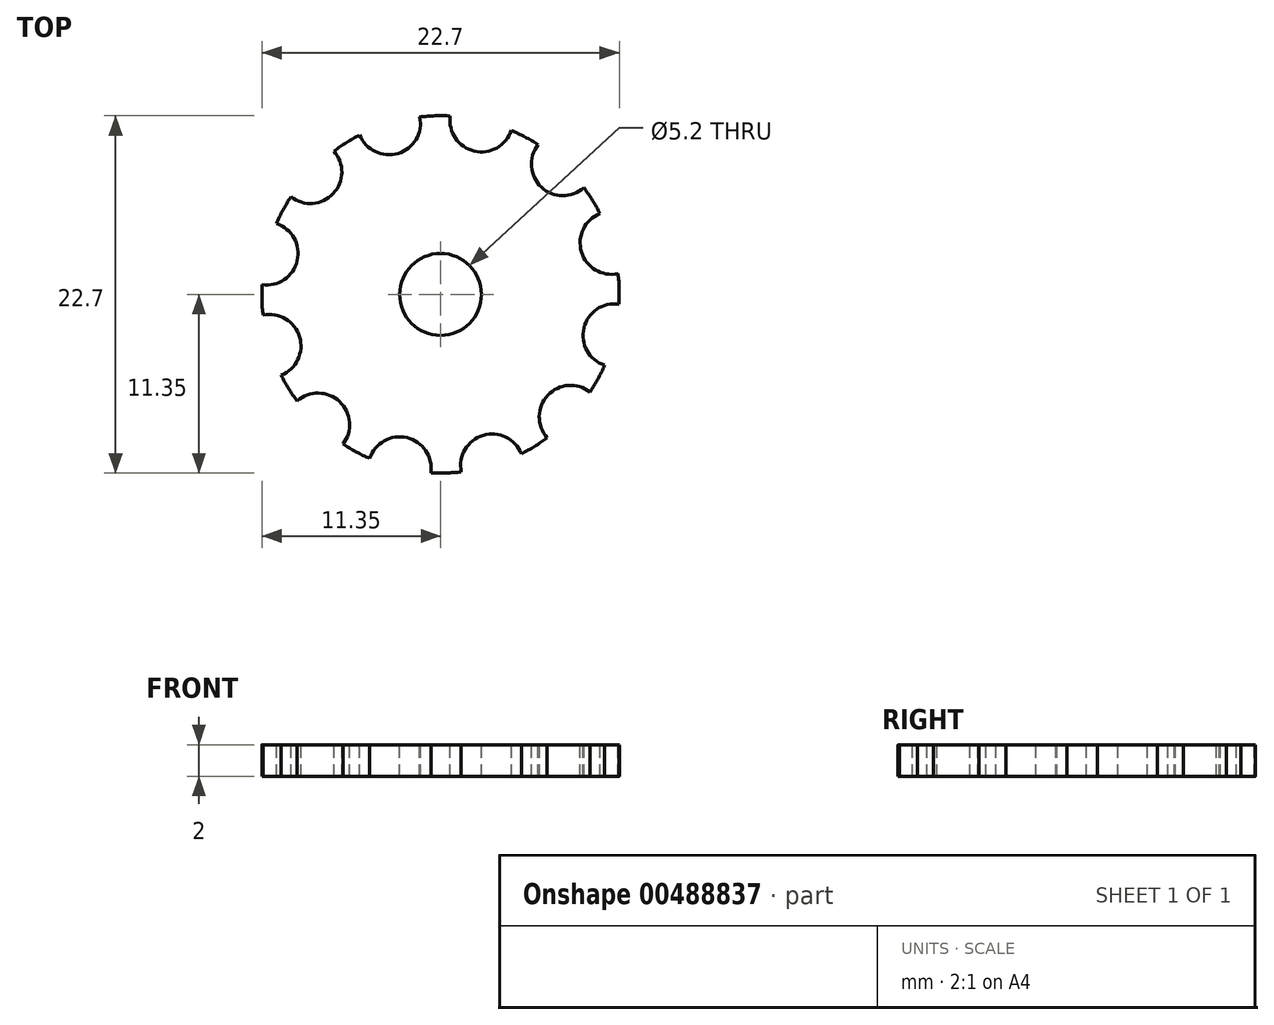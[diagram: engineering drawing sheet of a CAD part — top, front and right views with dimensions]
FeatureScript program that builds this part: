
annotation { "Feature Type Name" : "Feature", "Feature Type Description" : "" }
export const myFeature = defineFeature(function(context is Context, id is Id, definition is map)
    precondition{}
    {
        {
            var Q0;
            Q0=qCreatedBy(makeId("Top.planeOp"),FACE);
            var sketch = newSketch(context, id + "F0", { "sketchPlane" : qUnion([Q0])});
            skCircle(sketch, "E0", {"center": v(0, 0) * mm, "radius": 11.35 * mm});
            skSolve(sketch);
        }
        {
            var Q0;
            Q0=makeQuery(id+"F0.imprint","IMPRINT",FACE,{"disambiguationData":[TD([[makeQuery(id+"F0.imprint","IMPRINT",EDGE,{"derivedFrom":sQuery(id+"F0.wireOp",EDGE,"E0")}),1.0]])]});
            extrude(context, id + "F1", {"entities" : qUnion([Q0]), "depth" : 2 * mm});
        }
        {
            var Q0;
            Q0=makeQuery(id+"F1.opExtrude","CAP_FACE",FACE,{"disambiguationData":[OSD([sQuery(id+"F0.wireOp",EDGE,"E0")])],"isStart":false});
            var sketch = newSketch(context, id + "F2", { "sketchPlane" : qUnion([Q0])});
            skCircle(sketch, "E1", {"center": v(7.77, 8.27) * mm, "radius": 2 * mm});
            skCircle(sketch, "E2.1.0", {"center": v(2.6, 11.05) * mm, "radius": 2 * mm});
            skCircle(sketch, "E2.2.0", {"center": v(-3.28, 10.87) * mm, "radius": 2 * mm});
            skCircle(sketch, "E2.3.0", {"center": v(-8.27, 7.77) * mm, "radius": 2 * mm});
            skCircle(sketch, "E2.4.0", {"center": v(-11.05, 2.6) * mm, "radius": 2 * mm});
            skCircle(sketch, "E2.5.0", {"center": v(-10.87, -3.28) * mm, "radius": 2 * mm});
            skPoint(sketch, "E2.center", {"position": v(0, 0) * mm});
            skCircle(sketch, "E3.1.6.0", {"center": v(-7.77, -8.27) * mm, "radius": 2 * mm});
            skCircle(sketch, "E3.1.7.0", {"center": v(-2.6, -11.05) * mm, "radius": 2 * mm});
            skCircle(sketch, "E3.1.8.0", {"center": v(3.28, -10.87) * mm, "radius": 2 * mm});
            skCircle(sketch, "E3.1.9.0", {"center": v(8.27, -7.77) * mm, "radius": 2 * mm});
            skCircle(sketch, "E3.1.10.0", {"center": v(11.05, -2.6) * mm, "radius": 2 * mm});
            skCircle(sketch, "E3.1.11.0", {"center": v(10.87, 3.28) * mm, "radius": 2 * mm});
            skCircle(sketch, "E4", {"center": v(0, 0) * mm, "radius": 2.6 * mm});
            skSolve(sketch);
        }
        {
            var Q0;
            Q0=makeQuery(id+"F2.imprint","IMPRINT",FACE,{"disambiguationData":[TD([[makeQuery(id+"F2.imprint","IMPRINT",EDGE,{"derivedFrom":sQuery(id+"F2.wireOp",EDGE,"E2.7.0")}),1.0]])]});
            var Q1;
            Q1=makeQuery(id+"F2.imprint","IMPRINT",FACE,{"disambiguationData":[TD([[makeQuery(id+"F2.imprint","IMPRINT",EDGE,{"derivedFrom":sQuery(id+"F2.wireOp",EDGE,"E1")}),1.0]])]});
            var Q2;
            Q2=makeQuery(id+"F2.imprint","IMPRINT",FACE,{"disambiguationData":[TD([[makeQuery(id+"F2.imprint","IMPRINT",EDGE,{"derivedFrom":sQuery(id+"F2.wireOp",EDGE,"E2.1.0")}),1.0]])]});
            var Q3;
            Q3=makeQuery(id+"F2.imprint","IMPRINT",FACE,{"disambiguationData":[TD([[makeQuery(id+"F2.imprint","IMPRINT",EDGE,{"derivedFrom":sQuery(id+"F2.wireOp",EDGE,"E2.2.0")}),1.0]])]});
            var Q4;
            Q4=makeQuery(id+"F2.imprint","IMPRINT",FACE,{"disambiguationData":[TD([[makeQuery(id+"F2.imprint","IMPRINT",EDGE,{"derivedFrom":sQuery(id+"F2.wireOp",EDGE,"E2.3.0")}),1.0]])]});
            var Q5;
            Q5=makeQuery(id+"F2.imprint","IMPRINT",FACE,{"disambiguationData":[TD([[makeQuery(id+"F2.imprint","IMPRINT",EDGE,{"derivedFrom":sQuery(id+"F2.wireOp",EDGE,"E2.4.0")}),1.0]])]});
            var Q6;
            Q6=makeQuery(id+"F2.imprint","IMPRINT",FACE,{"disambiguationData":[TD([[makeQuery(id+"F2.imprint","IMPRINT",EDGE,{"derivedFrom":sQuery(id+"F2.wireOp",EDGE,"E2.6.0")}),1.0]])]});
            var Q7;
            Q7=makeQuery(id+"F2.imprint","IMPRINT",FACE,{"disambiguationData":[TD([[makeQuery(id+"F2.imprint","IMPRINT",EDGE,{"derivedFrom":sQuery(id+"F2.wireOp",EDGE,"E3.1.11.0")}),1.0]])]});
            var Q8;
            Q8=makeQuery(id+"F2.imprint","IMPRINT",FACE,{"disambiguationData":[TD([[makeQuery(id+"F2.imprint","IMPRINT",EDGE,{"derivedFrom":sQuery(id+"F2.wireOp",EDGE,"E3.1.10.0")}),1.0]])]});
            var Q9;
            Q9=makeQuery(id+"F2.imprint","IMPRINT",FACE,{"disambiguationData":[TD([[makeQuery(id+"F2.imprint","IMPRINT",EDGE,{"derivedFrom":sQuery(id+"F2.wireOp",EDGE,"E3.1.7.0")}),1.0]])]});
            var Q10;
            Q10=makeQuery(id+"F2.imprint","IMPRINT",FACE,{"disambiguationData":[TD([[makeQuery(id+"F2.imprint","IMPRINT",EDGE,{"derivedFrom":sQuery(id+"F2.wireOp",EDGE,"E2.5.0")}),1.0]])]});
            var Q11;
            Q11=makeQuery(id+"F2.imprint","IMPRINT",FACE,{"disambiguationData":[TD([[makeQuery(id+"F2.imprint","IMPRINT",EDGE,{"derivedFrom":sQuery(id+"F2.wireOp",EDGE,"E3.1.6.0")}),1.0]])]});
            var Q12;
            Q12=makeQuery(id+"F2.imprint","IMPRINT",FACE,{"disambiguationData":[TD([[makeQuery(id+"F2.imprint","IMPRINT",EDGE,{"derivedFrom":sQuery(id+"F2.wireOp",EDGE,"E3.1.9.0")}),1.0]])]});
            var Q13;
            Q13=makeQuery(id+"F2.imprint","IMPRINT",FACE,{"disambiguationData":[TD([[makeQuery(id+"F2.imprint","IMPRINT",EDGE,{"derivedFrom":sQuery(id+"F2.wireOp",EDGE,"E3.1.8.0")}),1.0]])]});
            var Q14;
            Q14=makeQuery(id+"F2.imprint","IMPRINT",FACE,{"disambiguationData":[TD([[makeQuery(id+"F2.imprint","IMPRINT",EDGE,{"derivedFrom":sQuery(id+"F2.wireOp",EDGE,"E4")}),1.0]])]});
            extrude(context, id + "F3", {"entities" : qUnion([Q0, Q1, Q2, Q3, Q4, Q5, Q6, Q7, Q8, Q9, Q10, Q11, Q12, Q13, Q14]), "operationType" : NewBodyOperationType.REMOVE, "oppositeDirection" : true, "depth" : 25 * mm});
        }
    });
